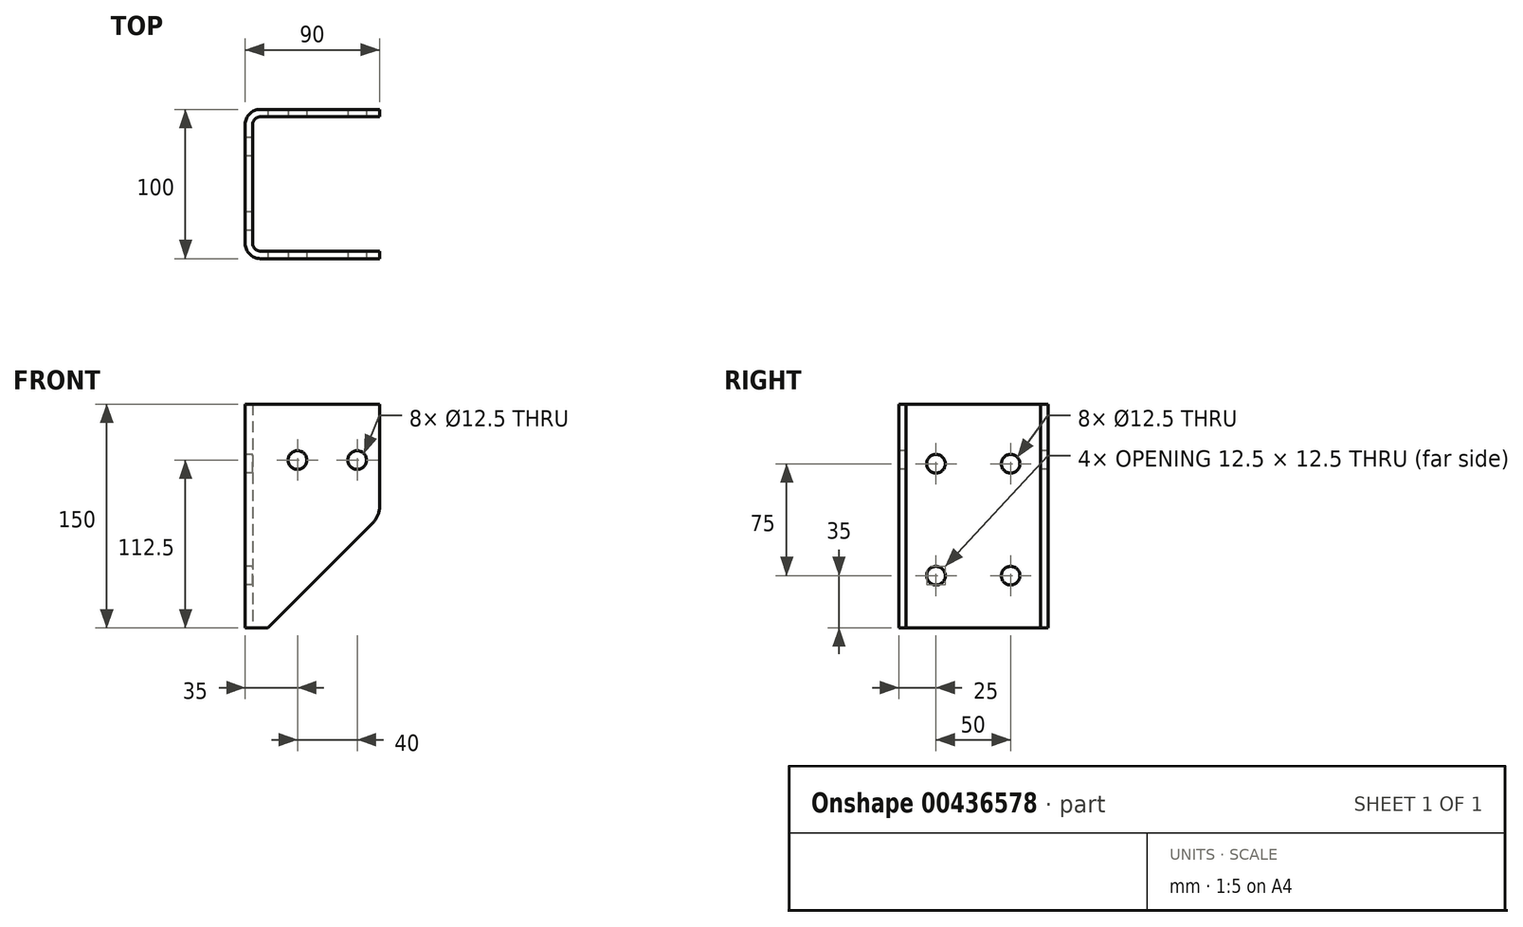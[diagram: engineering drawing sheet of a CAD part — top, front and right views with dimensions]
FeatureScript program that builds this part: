
annotation { "Feature Type Name" : "Feature", "Feature Type Description" : "" }
export const myFeature = defineFeature(function(context is Context, id is Id, definition is map)
    precondition{}
    {
        {
            var Q0;
            Q0=qCreatedBy(makeId("Top.planeOp"),FACE);
            var sketch = newSketch(context, id + "F0", { "sketchPlane" : qUnion([Q0])});
            skLineSegment(sketch, "E0.bottom", {"start": v(40, 50) * mm, "end": v(-40, 50) * mm});
            skLineSegment(sketch, "E0.top", {"start": v(40, -50) * mm, "end": v(-40, -50) * mm});
            skLineSegment(sketch, "E0.left", {"start": v(50, 40) * mm, "end": v(50, -40) * mm});
            skLineSegment(sketch, "E0.right", {"start": v(-50, 40) * mm, "end": v(-50, -40) * mm});
            skPoint(sketch, "E0.middle", {"position": v(0, 0) * mm});
            skPoint(sketch, "E1.visualSharp", {"position": v(-50, -50) * mm});
            skArc(sketch, "E1.filletArc", {"start": v(-50, -40) * mm, "mid": v(-47.07, -47.07) * mm, "end": v(-40, -50) * mm});
            skPoint(sketch, "E2.visualSharp", {"position": v(50, -50) * mm});
            skArc(sketch, "E2.filletArc", {"start": v(40, -50) * mm, "mid": v(47.07, -47.07) * mm, "end": v(50, -40) * mm});
            skPoint(sketch, "E3.visualSharp", {"position": v(50, 50) * mm});
            skArc(sketch, "E3.filletArc", {"start": v(50, 40) * mm, "mid": v(47.07, 47.07) * mm, "end": v(40, 50) * mm});
            skPoint(sketch, "E4.visualSharp", {"position": v(-50, 50) * mm});
            skArc(sketch, "E4.filletArc", {"start": v(-40, 50) * mm, "mid": v(-47.07, 47.07) * mm, "end": v(-50, 40) * mm});
            skArc(sketch, "E5.0", {"start": v(45, 40) * mm, "mid": v(43.54, 43.54) * mm, "end": v(40, 45) * mm});
            skLineSegment(sketch, "E5.1", {"start": v(45, 40) * mm, "end": v(45, -40) * mm});
            skLineSegment(sketch, "E5.2", {"start": v(40, 45) * mm, "end": v(-40, 45) * mm});
            skArc(sketch, "E5.3", {"start": v(40, -45) * mm, "mid": v(43.54, -43.54) * mm, "end": v(45, -40) * mm});
            skArc(sketch, "E5.4", {"start": v(-40, 45) * mm, "mid": v(-43.54, 43.54) * mm, "end": v(-45, 40) * mm});
            skLineSegment(sketch, "E5.5", {"start": v(-45, 40) * mm, "end": v(-45, -40) * mm});
            skArc(sketch, "E5.6", {"start": v(-45, -40) * mm, "mid": v(-43.54, -43.54) * mm, "end": v(-40, -45) * mm});
            skLineSegment(sketch, "E5.7", {"start": v(40, -45) * mm, "end": v(-40, -45) * mm});
            skSolve(sketch);
        }
        {
            var Q0;
            Q0 = qSketchRegion(id + "F0", true);
            extrude(context, id + "F1", {"entities" : qUnion([Q0]), "depth" : 150 * mm});
        }
        {
            var Q0;
            Q0=makeQuery(id+"F1.opExtrude","SWEPT_FACE",FACE,{"disambiguationData":[OSD([sQuery(id+"F0.wireOp",EDGE,"E0.top")])]});
            var sketch = newSketch(context, id + "F2", { "sketchPlane" : qUnion([Q0])});
            skLineSegment(sketch, "E6", {"start": v(40, 150) * mm, "end": v(40, 75) * mm});
            skLineSegment(sketch, "E7", {"start": v(40, 75) * mm, "end": v(-35, 0) * mm});
            skLineSegment(sketch, "E8", {"start": v(-35, 0) * mm, "end": v(50, 0) * mm});
            skLineSegment(sketch, "E9", {"start": v(50, 0) * mm, "end": v(50, 150) * mm});
            skLineSegment(sketch, "E10", {"start": v(50, 150) * mm, "end": v(40, 150) * mm});
            skCircle(sketch, "E11", {"center": v(-15, 112.5) * mm, "radius": 6.25 * mm});
            skCircle(sketch, "E12", {"center": v(25, 112.5) * mm, "radius": 6.25 * mm});
            skSolve(sketch);
        }
        {
            var Q0;
            Q0 = qSketchRegion(id + "F2", true);
            extrude(context, id + "F3", {"entities" : qUnion([Q0]), "operationType" : NewBodyOperationType.REMOVE, "endBound" : BoundingType.THROUGH_ALL, "oppositeDirection" : true, "depth" : 25 * mm});
        }
        {
            var Q0;
            Q0=makeQuery(id+"F1.opExtrude","SWEPT_FACE",FACE,{"disambiguationData":[OSD([sQuery(id+"F0.wireOp",EDGE,"E0.right")])]});
            var sketch = newSketch(context, id + "F4", { "sketchPlane" : qUnion([Q0])});
            skCircle(sketch, "E13", {"center": v(-25, 110) * mm, "radius": 6.25 * mm});
            skCircle(sketch, "E14", {"center": v(-25, 35) * mm, "radius": 6.25 * mm});
            skLineSegment(sketch, "E15", {"start": v(0, 150) * mm, "end": v(0, 0) * mm, "construction": true});
            skCircle(sketch, "E16.MirrorC", {"center": v(25, 35) * mm, "radius": 6.25 * mm});
            skCircle(sketch, "E17.MirrorC", {"center": v(25, 110) * mm, "radius": 6.25 * mm});
            skSolve(sketch);
        }
        {
            var Q0;
            Q0 = qSketchRegion(id + "F4", true);
            extrude(context, id + "F5", {"entities" : qUnion([Q0]), "operationType" : NewBodyOperationType.REMOVE, "endBound" : BoundingType.THROUGH_ALL, "oppositeDirection" : true, "depth" : 25 * mm});
        }
        {
            var Q0;
            {var subQ0=sQuery(id+"F0.wireOp",EDGE,"E0.top");var subQ1=sQuery(id+"F2.wireOp",EDGE,"E6");var subQ2=sQuery(id+"F2.wireOp",EDGE,"E7");Q0=makeQuery(id+"F3.boolean.opBoolean","COPY",EDGE,{"disambiguationData":[TD([makeQuery(id+"F1.opExtrude","SWEPT_FACE",FACE,{"disambiguationData":[OSD([subQ0])]})])],"derivedFrom":makeQuery(id+"F3.opExtrude","SWEPT_EDGE",EDGE,{"disambiguationData":[OSD([subQ0,sQuery(id+"F0.wireOp",EDGE,"E2.filletArc"),subQ1,subQ2])]})});}
            var Q1;
            {var subQ1=sQuery(id+"F0.wireOp",EDGE,"E0.top");var subQ2=sQuery(id+"F2.wireOp",EDGE,"E6");Q1=makeQuery(id+"F3.boolean.opBoolean","COPY",EDGE,{"disambiguationData":[TD([makeQuery(id+"F1.opExtrude","SWEPT_FACE",FACE,{"disambiguationData":[OSD([subQ1])]})])],"derivedFrom":makeQuery(id+"F3.opExtrude","SWEPT_EDGE",EDGE,{"disambiguationData":[OSD([subQ1,subQ2,sQuery(id+"F2.wireOp",EDGE,"E10")])]})});}
            var Q2;
            {var subQ0=sQuery(id+"F0.wireOp",EDGE,"E0.bottom");var subQ2=sQuery(id+"F0.wireOp",EDGE,"E0.top");var subQ3=sQuery(id+"F2.wireOp",EDGE,"E6");Q2=makeQuery(id+"F3.boolean.opBoolean","COPY",EDGE,{"disambiguationData":[TD([makeQuery(id+"F1.opExtrude","SWEPT_FACE",FACE,{"disambiguationData":[OSD([subQ0])]})])],"derivedFrom":makeQuery(id+"F3.opExtrude","SWEPT_EDGE",EDGE,{"disambiguationData":[OSD([subQ2,subQ3,sQuery(id+"F2.wireOp",EDGE,"E10")])]})});}
            var Q3;
            {var subQ0=sQuery(id+"F2.wireOp",EDGE,"E6");var subQ1=sQuery(id+"F2.wireOp",EDGE,"E7");Q3=makeQuery(id+"F3.boolean.opBoolean","COPY",EDGE,{"disambiguationData":[TD([makeQuery(id+"F1.opExtrude","SWEPT_FACE",FACE,{"disambiguationData":[OSD([sQuery(id+"F0.wireOp",EDGE,"E0.bottom")])]})])],"derivedFrom":makeQuery(id+"F3.opExtrude","SWEPT_EDGE",EDGE,{"disambiguationData":[OSD([sQuery(id+"F0.wireOp",EDGE,"E0.top"),sQuery(id+"F0.wireOp",EDGE,"E2.filletArc"),subQ0,subQ1])]})});}
            fillet(context, id + "F6", {"entities" : qUnion([Q0, Q1, Q2, Q3]), "radius" : 15 * mm, "tangentPropagation" : true, "allowEdgeOverflow" : false});
        }
    });
